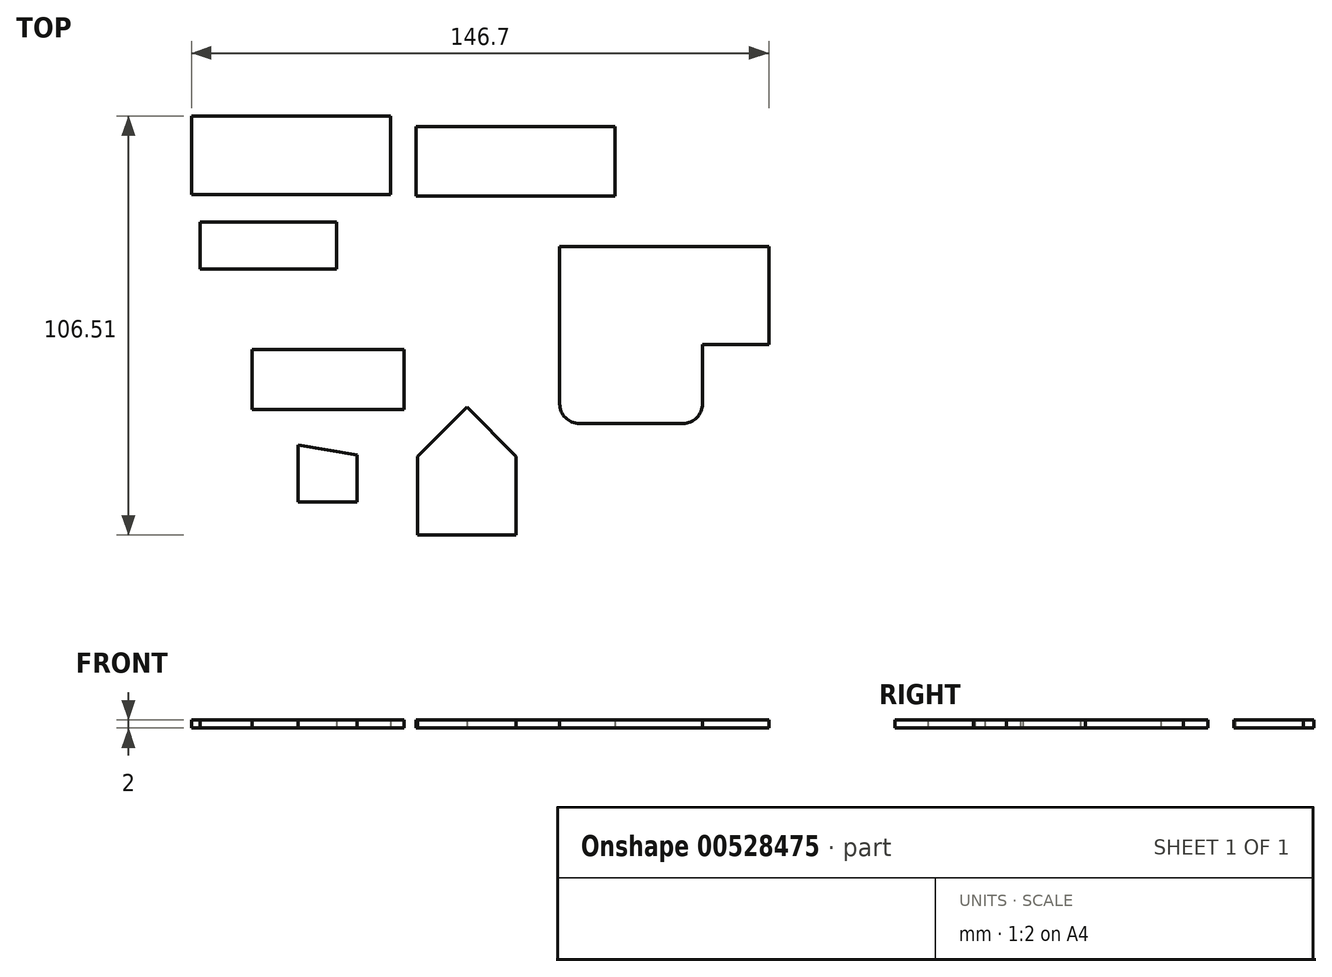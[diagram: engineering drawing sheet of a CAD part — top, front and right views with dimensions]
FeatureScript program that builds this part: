
annotation { "Feature Type Name" : "Feature", "Feature Type Description" : "" }
export const myFeature = defineFeature(function(context is Context, id is Id, definition is map)
    precondition{}
    {
        {
            var Q0;
            Q0=qCreatedBy(makeId("Top.planeOp"),FACE);
            var sketch = newSketch(context, id + "F0", { "sketchPlane" : qUnion([Q0])});
            skLineSegment(sketch, "E0.bottom", {"start": v(-93.57, 51.9) * mm, "end": v(-42.98, 51.9) * mm});
            skLineSegment(sketch, "E0.top", {"start": v(-93.57, 31.9) * mm, "end": v(-42.98, 31.9) * mm});
            skLineSegment(sketch, "E0.left", {"start": v(-93.57, 51.9) * mm, "end": v(-93.57, 31.9) * mm});
            skLineSegment(sketch, "E0.right", {"start": v(-42.98, 51.9) * mm, "end": v(-42.98, 31.9) * mm});
            skSolve(sketch);
        }
        {
            var Q0;
            Q0=makeQuery(id+"F0.imprint","IMPRINT",FACE,{"disambiguationData":[TD([[makeQuery(id+"F0.imprint","IMPRINT",EDGE,{"derivedFrom":sQuery(id+"F0.wireOp",EDGE,"E0.bottom")}),-1.0]])]});
            extrude(context, id + "F1", {"entities" : qUnion([Q0]), "depth" : 2 * mm, "offsetDistance" : 25 * mm});
        }
        {
            var Q0;
            Q0=qCreatedBy(makeId("Top.planeOp"),FACE);
            var sketch = newSketch(context, id + "F2", { "sketchPlane" : qUnion([Q0])});
            skLineSegment(sketch, "E1.bottom", {"start": v(-91.3, 24.97) * mm, "end": v(-56.7, 24.97) * mm});
            skLineSegment(sketch, "E1.top", {"start": v(-91.3, 12.97) * mm, "end": v(-56.7, 12.97) * mm});
            skLineSegment(sketch, "E1.left", {"start": v(-91.3, 24.97) * mm, "end": v(-91.3, 12.97) * mm});
            skLineSegment(sketch, "E1.right", {"start": v(-56.7, 24.97) * mm, "end": v(-56.7, 12.97) * mm});
            skSolve(sketch);
        }
        {
            var Q0;
            Q0=makeQuery(id+"F2.imprint","IMPRINT",FACE,{"disambiguationData":[TD([[makeQuery(id+"F2.imprint","IMPRINT",EDGE,{"derivedFrom":sQuery(id+"F2.wireOp",EDGE,"E1.bottom")}),-1.0]])]});
            extrude(context, id + "F3", {"entities" : qUnion([Q0]), "depth" : 2 * mm, "offsetDistance" : 25 * mm});
        }
        {
            var Q0;
            Q0=qCreatedBy(makeId("Top.planeOp"),FACE);
            var sketch = newSketch(context, id + "F4", { "sketchPlane" : qUnion([Q0])});
            skLineSegment(sketch, "E2.bottom", {"start": v(-36.51, 49.17) * mm, "end": v(14.08, 49.17) * mm});
            skLineSegment(sketch, "E2.top", {"start": v(-36.51, 31.5) * mm, "end": v(14.08, 31.5) * mm});
            skLineSegment(sketch, "E2.left", {"start": v(-36.51, 49.17) * mm, "end": v(-36.51, 31.5) * mm});
            skLineSegment(sketch, "E2.right", {"start": v(14.08, 49.17) * mm, "end": v(14.08, 31.5) * mm});
            skSolve(sketch);
        }
        {
            var Q0;
            Q0=makeQuery(id+"F4.imprint","IMPRINT",FACE,{"disambiguationData":[TD([[makeQuery(id+"F4.imprint","IMPRINT",EDGE,{"derivedFrom":sQuery(id+"F4.wireOp",EDGE,"E2.bottom")}),-1.0]])]});
            extrude(context, id + "F5", {"entities" : qUnion([Q0]), "depth" : 2 * mm, "offsetDistance" : 25 * mm});
        }
        {
            var Q0;
            Q0=qCreatedBy(makeId("Top.planeOp"),FACE);
            var sketch = newSketch(context, id + "F6", { "sketchPlane" : qUnion([Q0])});
            skLineSegment(sketch, "E3.bottom", {"start": v(0, 18.77) * mm, "end": v(53.13, 18.77) * mm});
            skLineSegment(sketch, "E3.top", {"start": v(0, -6.23) * mm, "end": v(53.13, -6.23) * mm});
            skLineSegment(sketch, "E3.left", {"start": v(0, 18.77) * mm, "end": v(0, -6.23) * mm});
            skLineSegment(sketch, "E3.right", {"start": v(53.13, 18.77) * mm, "end": v(53.13, -6.23) * mm});
            skLineSegment(sketch, "E4.bottom", {"start": v(0, -6.23) * mm, "end": v(36.3, -6.23) * mm});
            skLineSegment(sketch, "E4.top", {"start": v(5, -26.23) * mm, "end": v(31.3, -26.23) * mm});
            skLineSegment(sketch, "E4.left", {"start": v(0, -6.23) * mm, "end": v(0, -21.23) * mm});
            skLineSegment(sketch, "E4.right", {"start": v(36.3, -6.23) * mm, "end": v(36.3, -21.23) * mm});
            skPoint(sketch, "E5.visualSharp", {"position": v(0, -26.23) * mm});
            skArc(sketch, "E5.filletArc", {"start": v(0, -21.23) * mm, "mid": v(1.46, -24.77) * mm, "end": v(5, -26.23) * mm});
            skPoint(sketch, "E6.visualSharp", {"position": v(36.3, -26.23) * mm});
            skArc(sketch, "E6.filletArc", {"start": v(31.3, -26.23) * mm, "mid": v(34.83, -24.77) * mm, "end": v(36.3, -21.23) * mm});
            skSolve(sketch);
        }
        {
            var Q0;
            Q0 = qSketchRegion(id + "F6", true);
            extrude(context, id + "F7", {"entities" : qUnion([Q0]), "depth" : 2 * mm, "offsetDistance" : 25 * mm});
        }
        {
            var Q0;
            Q0=qCreatedBy(makeId("Top.planeOp"),FACE);
            var sketch = newSketch(context, id + "F8", { "sketchPlane" : qUnion([Q0])});
            skLineSegment(sketch, "E7.bottom", {"start": v(-78.15, -7.5) * mm, "end": v(-39.54, -7.5) * mm});
            skLineSegment(sketch, "E7.top", {"start": v(-78.15, -22.7) * mm, "end": v(-39.54, -22.7) * mm});
            skLineSegment(sketch, "E7.left", {"start": v(-78.15, -7.5) * mm, "end": v(-78.15, -22.7) * mm});
            skLineSegment(sketch, "E7.right", {"start": v(-39.54, -7.5) * mm, "end": v(-39.54, -22.7) * mm});
            skSolve(sketch);
        }
        {
            var Q0;
            Q0=qCreatedBy(makeId("Top.planeOp"),FACE);
            var sketch = newSketch(context, id + "F9", { "sketchPlane" : qUnion([Q0])});
            skLineSegment(sketch, "E8.bottom", {"start": v(-66.47, -34.21) * mm, "end": v(-51.47, -34.21) * mm});
            skLineSegment(sketch, "E8.top", {"start": v(-66.47, -46.21) * mm, "end": v(-51.47, -46.21) * mm});
            skLineSegment(sketch, "E8.left", {"start": v(-66.47, -34.21) * mm, "end": v(-66.47, -46.21) * mm});
            skLineSegment(sketch, "E8.right", {"start": v(-51.47, -34.21) * mm, "end": v(-51.47, -46.21) * mm});
            skLineSegment(sketch, "E9", {"start": v(-66.47, -34.21) * mm, "end": v(-66.47, -31.71) * mm});
            skLineSegment(sketch, "E10", {"start": v(-51.47, -34.21) * mm, "end": v(-66.47, -31.71) * mm});
            skSolve(sketch);
        }
        {
            var Q0;
            Q0 = qSketchRegion(id + "F8", true);
            extrude(context, id + "F10", {"entities" : qUnion([Q0]), "depth" : 2 * mm, "offsetDistance" : 25 * mm});
        }
        {
            var Q0;
            Q0 = qSketchRegion(id + "F9", true);
            extrude(context, id + "F11", {"entities" : qUnion([Q0]), "depth" : 2 * mm, "offsetDistance" : 25 * mm});
        }
        {
            var Q0;
            Q0=qCreatedBy(makeId("Top.planeOp"),FACE);
            var sketch = newSketch(context, id + "F12", { "sketchPlane" : qUnion([Q0])});
            skLineSegment(sketch, "E11.bottom", {"start": v(-36.08, -34.6) * mm, "end": v(-11.08, -34.6) * mm});
            skLineSegment(sketch, "E11.top", {"start": v(-36.08, -54.6) * mm, "end": v(-11.08, -54.6) * mm});
            skLineSegment(sketch, "E11.left", {"start": v(-36.08, -34.6) * mm, "end": v(-36.08, -54.6) * mm});
            skLineSegment(sketch, "E11.right", {"start": v(-11.08, -34.6) * mm, "end": v(-11.08, -54.6) * mm});
            skLineSegment(sketch, "E12", {"start": v(-36.08, -34.6) * mm, "end": v(-23.58, -34.6) * mm});
            skLineSegment(sketch, "E13", {"start": v(-23.58, -22.1) * mm, "end": v(-36.08, -34.6) * mm});
            skLineSegment(sketch, "E14", {"start": v(-23.58, -22.1) * mm, "end": v(-11.08, -34.6) * mm});
            skSolve(sketch);
        }
        {
            var Q0;
            Q0 = qSketchRegion(id + "F12", true);
            extrude(context, id + "F13", {"entities" : qUnion([Q0]), "depth" : 2 * mm, "offsetDistance" : 25 * mm});
        }
    });
